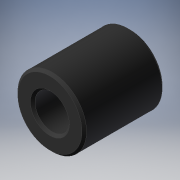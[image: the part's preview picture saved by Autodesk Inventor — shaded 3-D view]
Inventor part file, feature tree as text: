
AUTODESK INVENTOR PART (.ipt)
format: ipt  version: 2019 (Build 230136000, 136)  size: 151,552 bytes
history: native  units: mm
features: other x14, revolve x5, hole x1, sketch x1
ambient origin geometry x8: Origin, YZ Plane, XZ Plane, XY Plane, X Axis, Y Axis, Z Axis, Center Point
bodies: Solid1 (feature_tree)
feature tree (21):
  revolve  "Revolution1"  Angle=360.0deg
  revolve  "Revolution2"  Angle=360.0deg
  revolve  "Revolution3"  Angle=360.0deg
  hole  "Hole1"  [1 undecoded]
  revolve  "Revolution4"  [1 undecoded]
  revolve  "Revolution5"  [1 undecoded]
  other  "spring_XY"
  other  "spring_YZ"
  other  "spring_ZX"
  other  "spring_X"
  other  "spring_Y"
  other  "spring_Z"
  other  "spring_Center"
  other  "to_bolt_XY"
  other  "to_bolt_YZ"
  other  "to_bolt_ZX"
  other  "to_bolt_X"
  other  "to_bolt_Y"
  other  "to_bolt_Z"
  other  "to_bolt_Center"
  sketch  "Sketch4"  dims[d0=360.0deg d1=360.0deg d2=360.0deg d3=3.0mm d4=6.0mm d5=4.0mm d6=2.0mm d7=90.0deg d8=7.0mm d9=0.0mm d10=360.0deg d11=360.0deg d12=0.0mm d13=0.0mm]
note: 3 required parameter values undecoded (feature->parameter linkage not recoverable at this tier; creation-order binding heuristic only, values carry confidence <= 0.55)